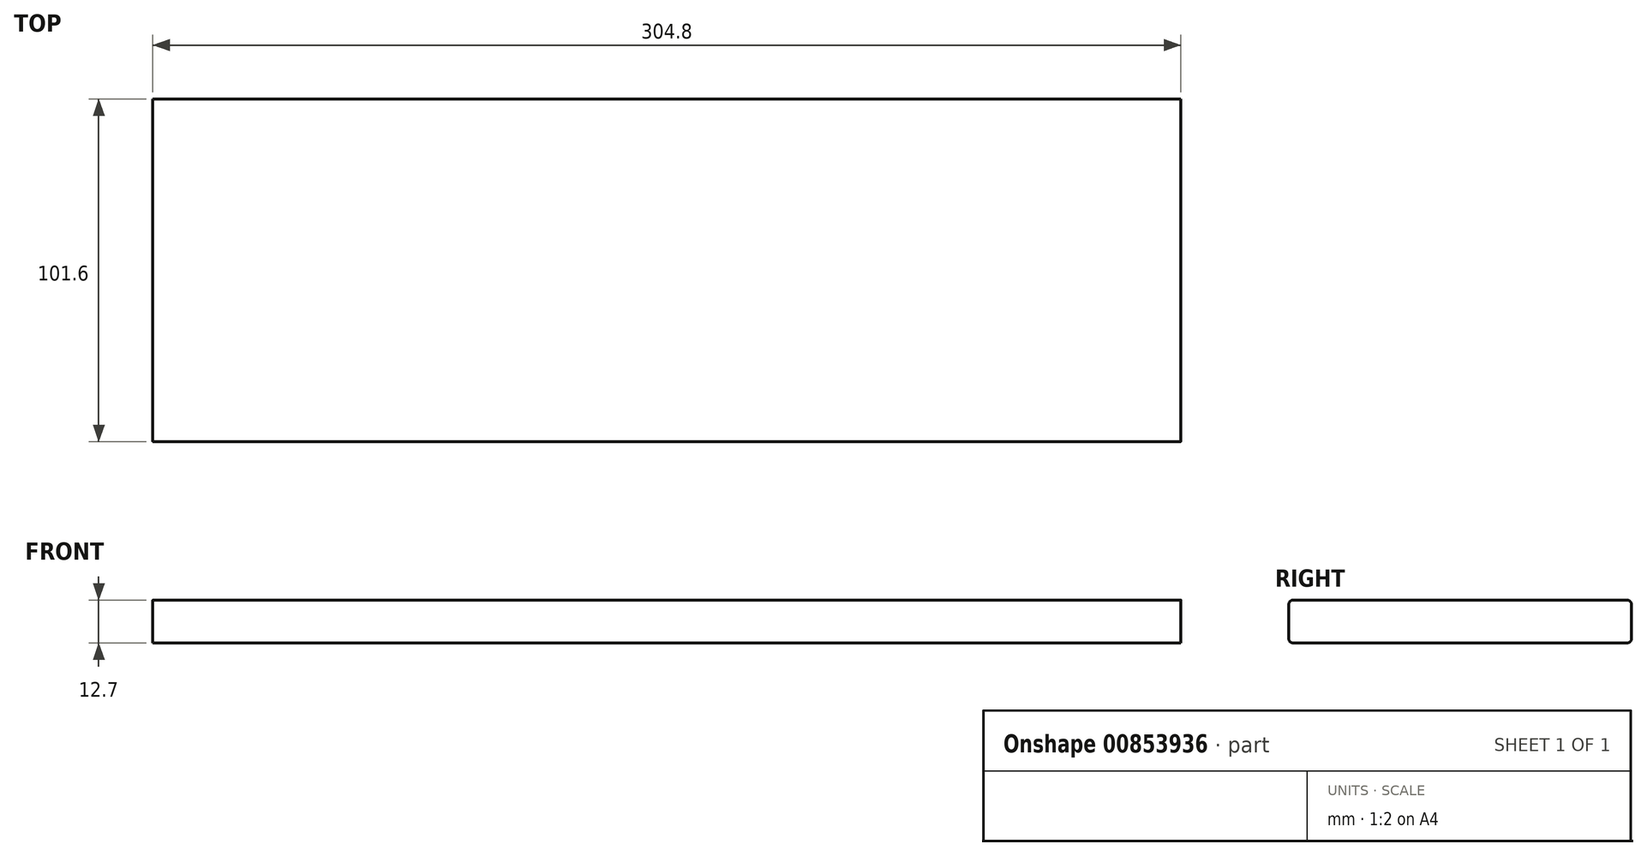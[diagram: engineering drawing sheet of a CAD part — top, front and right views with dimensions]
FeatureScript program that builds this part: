
annotation { "Feature Type Name" : "Feature", "Feature Type Description" : "" }
export const myFeature = defineFeature(function(context is Context, id is Id, definition is map)
    precondition{}
    {
        {
            var Q0;
            Q0=qCreatedBy(makeId("Front.planeOp"),FACE);
            var Q1;
            Q1=qCreatedBy(makeId("Front.planeOp"),FACE);
            var Q2;
            Q2=qCreatedBy(makeId("Front.planeOp"),FACE);
            var sketch = newSketch(context, id + "F0", { "sketchPlane" : qUnion([Q0, Q1, Q2])});
            skLineSegment(sketch, "E0.bottom", {"start": v(152.4, 6.35) * mm, "end": v(-152.4, 6.35) * mm});
            skLineSegment(sketch, "E0.top", {"start": v(152.4, -6.35) * mm, "end": v(-152.4, -6.35) * mm});
            skLineSegment(sketch, "E0.left", {"start": v(152.4, 6.35) * mm, "end": v(152.4, -6.35) * mm});
            skLineSegment(sketch, "E0.right", {"start": v(-152.4, 6.35) * mm, "end": v(-152.4, -6.35) * mm});
            skPoint(sketch, "E0.middle", {"position": v(0, 0) * mm});
            skSolve(sketch);
        }
        {
            var Q0;
            Q0=makeQuery(id+"F0.imprint","IMPRINT",FACE,{"disambiguationData":[TD([[makeQuery(id+"F0.imprint","IMPRINT",EDGE,{"derivedFrom":sQuery(id+"F0.wireOp",EDGE,"E0.bottom")}),1.0]])]});
            extrude(context, id + "F1", {"entities" : qUnion([Q0]), "flatOperationType" : FlatOperationType.REMOVE, "endBound" : BoundingType.SYMMETRIC, "depth" : 101.6 * mm, "offsetDistance" : 25.4 * mm, "domain" : OperationDomain.MODEL});
        }
        {
            var Q0;
            Q0=makeQuery(id+"F1.opExtrude","CAP_EDGE",EDGE,{"disambiguationData":[OSD([sQuery(id+"F0.wireOp",EDGE,"E0.bottom")])],"isStart":false});
            var Q1;
            Q1=makeQuery(id+"F1.opExtrude","CAP_EDGE",EDGE,{"disambiguationData":[OSD([sQuery(id+"F0.wireOp",EDGE,"E0.bottom")])],"isStart":true});
            var Q2;
            Q2=makeQuery(id+"F1.opExtrude","CAP_EDGE",EDGE,{"disambiguationData":[OSD([sQuery(id+"F0.wireOp",EDGE,"E0.top")])],"isStart":false});
            var Q3;
            Q3=makeQuery(id+"F1.opExtrude","CAP_EDGE",EDGE,{"disambiguationData":[OSD([sQuery(id+"F0.wireOp",EDGE,"E0.top")])],"isStart":true});
            fillet(context, id + "F2", {"entities" : qUnion([Q0, Q1, Q2, Q3]), "radius" : 1.27 * mm, "tangentPropagation" : true, "allowEdgeOverflow" : false});
        }
    });
